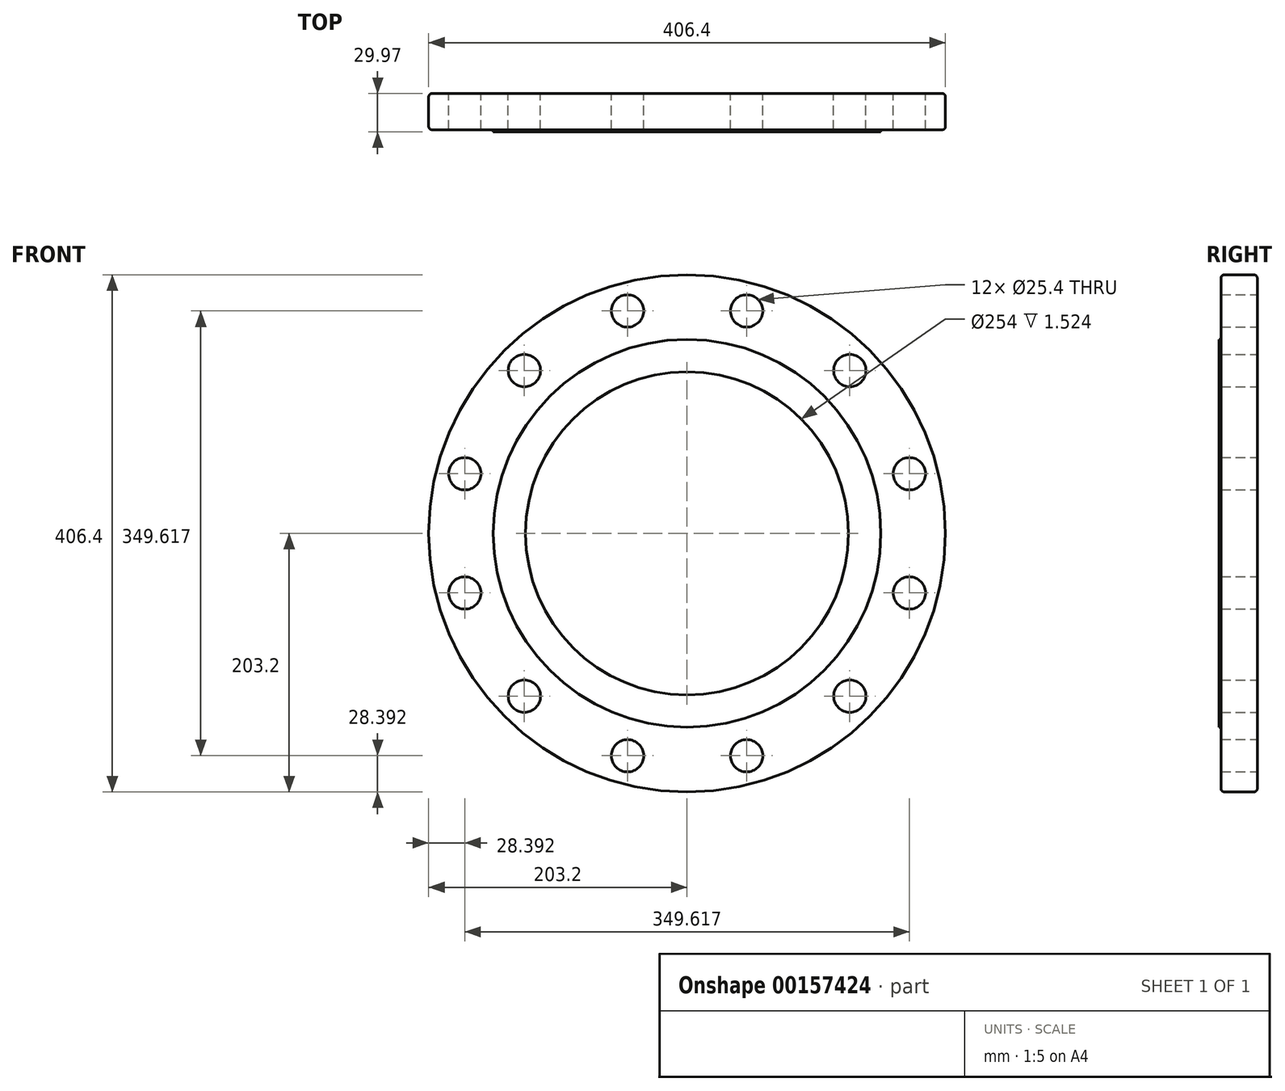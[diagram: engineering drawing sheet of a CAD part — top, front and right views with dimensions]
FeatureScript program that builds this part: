
annotation { "Feature Type Name" : "Feature", "Feature Type Description" : "" }
export const myFeature = defineFeature(function(context is Context, id is Id, definition is map)
    precondition{}
    {
        {
            var Q0;
            Q0=qCreatedBy(makeId("Front.planeOp"),FACE);
            var sketch = newSketch(context, id + "F0", { "sketchPlane" : qUnion([Q0])});
            skCircle(sketch, "E0", {"center": v(0, 0) * mm, "radius": 203.2 * mm});
            skLineSegment(sketch, "E1", {"start": v(0, 0) * mm, "end": v(0, 225.6) * mm});
            skLineSegment(sketch, "E2", {"start": v(0, 0) * mm, "end": v(59.02, 220.25) * mm});
            skCircle(sketch, "E3", {"center": v(46.84, 174.8) * mm, "radius": 12.7 * mm});
            skCircle(sketch, "E4.1.0", {"center": v(-46.84, 174.8) * mm, "radius": 12.7 * mm});
            skCircle(sketch, "E4.2.0", {"center": v(-127.97, 127.97) * mm, "radius": 12.7 * mm});
            skCircle(sketch, "E4.3.0", {"center": v(-174.8, 46.84) * mm, "radius": 12.7 * mm});
            skCircle(sketch, "E4.4.0", {"center": v(-174.8, -46.84) * mm, "radius": 12.7 * mm});
            skCircle(sketch, "E4.5.0", {"center": v(-127.97, -127.97) * mm, "radius": 12.7 * mm});
            skCircle(sketch, "E4.6.0", {"center": v(-46.84, -174.8) * mm, "radius": 12.7 * mm});
            skCircle(sketch, "E4.7.0", {"center": v(46.84, -174.8) * mm, "radius": 12.7 * mm});
            skCircle(sketch, "E4.8.0", {"center": v(127.97, -127.97) * mm, "radius": 12.7 * mm});
            skCircle(sketch, "E4.9.0", {"center": v(174.8, -46.84) * mm, "radius": 12.7 * mm});
            skCircle(sketch, "E4.10.0", {"center": v(174.8, 46.84) * mm, "radius": 12.7 * mm});
            skCircle(sketch, "E4.11.0", {"center": v(127.97, 127.97) * mm, "radius": 12.7 * mm});
            skSolve(sketch);
        }
        {
            var Q0;
            Q0=qSketchRegion(id+"F0",true);
            extrude(context, id + "F1", {"entities" : qUnion([Q0]), "depth" : 28.45 * mm});
        }
        {
            var Q0;
            Q0=makeQuery(id+"F1.opExtrude","CAP_EDGE",EDGE,{"disambiguationData":[OSD([sQuery(id+"F0.wireOp",EDGE,"E0")])],"isStart":false});
            var Q1;
            Q1=makeQuery(id+"F1.opExtrude","CAP_EDGE",EDGE,{"disambiguationData":[OSD([sQuery(id+"F0.wireOp",EDGE,"E0")])],"isStart":true});
            fillet(context, id + "F2", {"entities" : qUnion([Q0, Q1]), "radius" : 2.54 * mm, "tangentPropagation" : true, "allowEdgeOverflow" : false});
        }
        {
            var Q0;
            Q0=makeQuery(id+"F1.opExtrude","CAP_FACE",FACE,{"disambiguationData":[OSD([sQuery(id+"F0.wireOp",EDGE,"E0"),sQuery(id+"F0.wireOp",EDGE,"l6Qc9vSS-8Wm6-PDrN-dZje-1rI8Puq957m7"),sQuery(id+"F0.wireOp",EDGE,"E3"),sQuery(id+"F0.wireOp",EDGE,"E4.1.0"),sQuery(id+"F0.wireOp",EDGE,"E4.2.0"),sQuery(id+"F0.wireOp",EDGE,"E4.3.0"),sQuery(id+"F0.wireOp",EDGE,"E4.4.0"),sQuery(id+"F0.wireOp",EDGE,"E4.5.0"),sQuery(id+"F0.wireOp",EDGE,"E4.6.0"),sQuery(id+"F0.wireOp",EDGE,"E4.7.0"),sQuery(id+"F0.wireOp",EDGE,"E4.8.0"),sQuery(id+"F0.wireOp",EDGE,"E4.9.0"),sQuery(id+"F0.wireOp",EDGE,"E4.10.0"),sQuery(id+"F0.wireOp",EDGE,"E4.11.0")])],"isStart":false});
            var sketch = newSketch(context, id + "F3", { "sketchPlane" : qUnion([Q0])});
            skCircle(sketch, "E5", {"center": v(0, 0) * mm, "radius": 152.4 * mm});
            skCircle(sketch, "E6", {"center": v(0, 0) * mm, "radius": 127 * mm});
            skSolve(sketch);
        }
        {
            var Q0;
            Q0=qSketchRegion(id+"F3",true);
            extrude(context, id + "F4", {"entities" : qUnion([Q0]), "operationType" : NewBodyOperationType.ADD, "depth" : 1.52 * mm});
        }
    });
